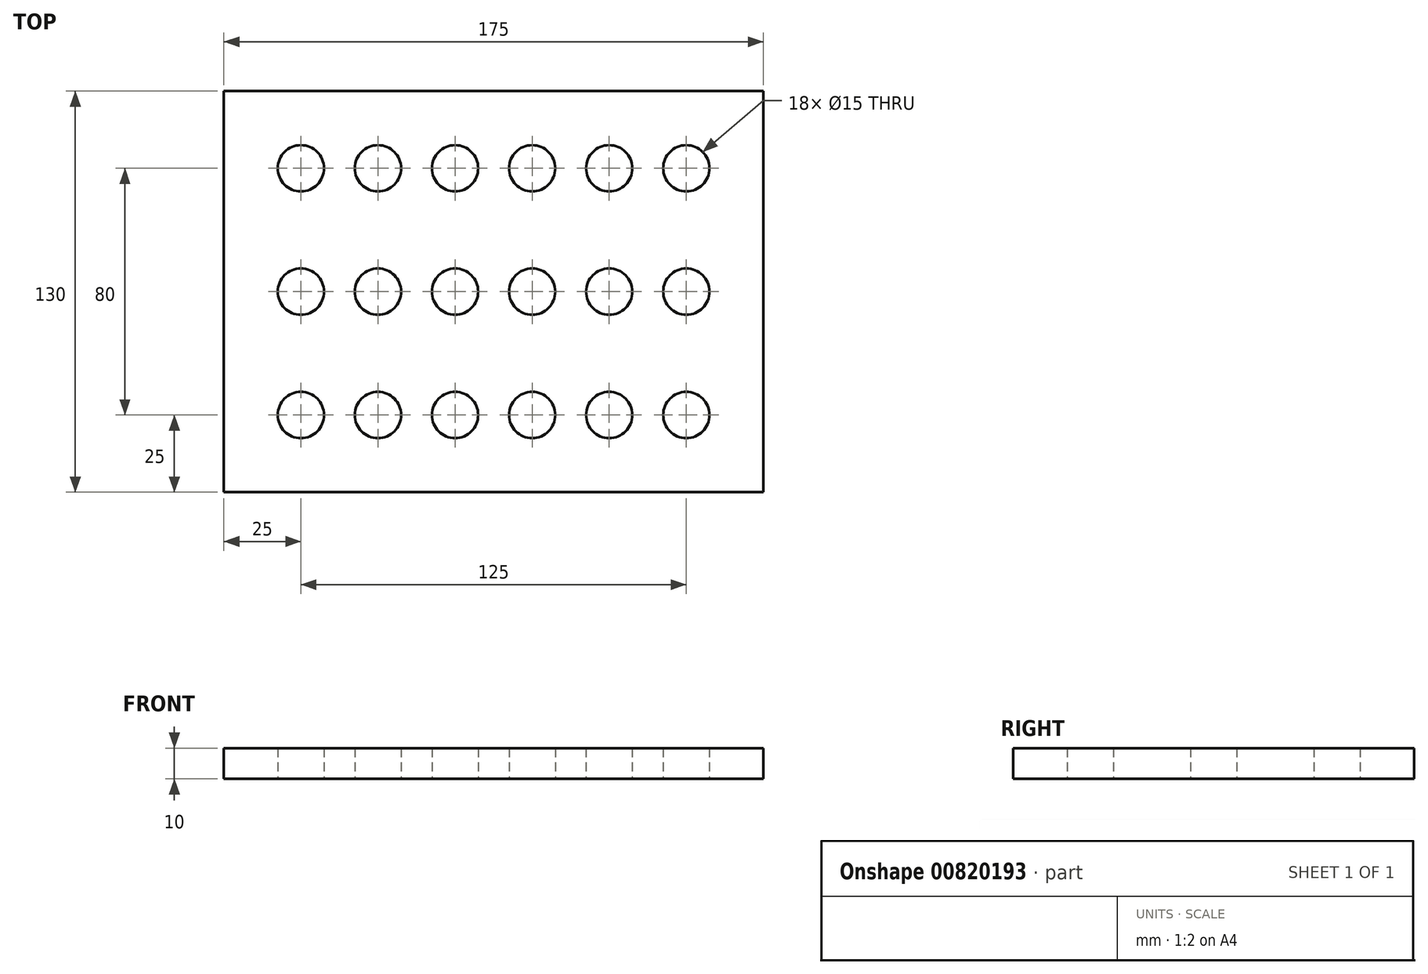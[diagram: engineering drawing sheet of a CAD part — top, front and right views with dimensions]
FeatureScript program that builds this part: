
annotation { "Feature Type Name" : "Feature", "Feature Type Description" : "" }
export const myFeature = defineFeature(function(context is Context, id is Id, definition is map)
    precondition{}
    {
        {
            var Q0;
            Q0=qCreatedBy(makeId("Top.planeOp"),FACE);
            var sketch = newSketch(context, id + "F0", { "sketchPlane" : qUnion([Q0])});
            skLineSegment(sketch, "E0.bottom", {"start": v(-87.5, 65) * mm, "end": v(87.5, 65) * mm});
            skLineSegment(sketch, "E0.top", {"start": v(-87.5, -65) * mm, "end": v(87.5, -65) * mm});
            skLineSegment(sketch, "E0.left", {"start": v(-87.5, 65) * mm, "end": v(-87.5, -65) * mm});
            skLineSegment(sketch, "E0.right", {"start": v(87.5, 65) * mm, "end": v(87.5, -65) * mm});
            skPoint(sketch, "E0.middle", {"position": v(0, 0) * mm});
            skCircle(sketch, "E1", {"center": v(-62.5, 40) * mm, "radius": 7.5 * mm});
            skCircle(sketch, "E2.0.1.0", {"center": v(-62.5, 0) * mm, "radius": 7.5 * mm});
            skCircle(sketch, "E2.0.2.0", {"center": v(-62.5, -40) * mm, "radius": 7.5 * mm});
            skCircle(sketch, "E2.1.0.0", {"center": v(-37.5, 40) * mm, "radius": 7.5 * mm});
            skCircle(sketch, "E2.1.1.0", {"center": v(-37.5, 0) * mm, "radius": 7.5 * mm});
            skCircle(sketch, "E2.1.2.0", {"center": v(-37.5, -40) * mm, "radius": 7.5 * mm});
            skCircle(sketch, "E2.2.0.0", {"center": v(-12.5, 40) * mm, "radius": 7.5 * mm});
            skCircle(sketch, "E2.2.1.0", {"center": v(-12.5, 0) * mm, "radius": 7.5 * mm});
            skCircle(sketch, "E2.2.2.0", {"center": v(-12.5, -40) * mm, "radius": 7.5 * mm});
            skCircle(sketch, "E2.3.0.0", {"center": v(12.5, 40) * mm, "radius": 7.5 * mm});
            skCircle(sketch, "E2.3.1.0", {"center": v(12.5, 0) * mm, "radius": 7.5 * mm});
            skCircle(sketch, "E2.3.2.0", {"center": v(12.5, -40) * mm, "radius": 7.5 * mm});
            skCircle(sketch, "E2.4.0.0", {"center": v(37.5, 40) * mm, "radius": 7.5 * mm});
            skCircle(sketch, "E2.4.1.0", {"center": v(37.5, 0) * mm, "radius": 7.5 * mm});
            skCircle(sketch, "E2.4.2.0", {"center": v(37.5, -40) * mm, "radius": 7.5 * mm});
            skCircle(sketch, "E2.5.0.0", {"center": v(62.5, 40) * mm, "radius": 7.5 * mm});
            skCircle(sketch, "E2.5.1.0", {"center": v(62.5, 0) * mm, "radius": 7.5 * mm});
            skCircle(sketch, "E2.5.2.0", {"center": v(62.5, -40) * mm, "radius": 7.5 * mm});
            skLineSegment(sketch, "E2.direction1", {"start": v(-62.5, 40) * mm, "end": v(-37.5, 40) * mm, "construction": true});
            skLineSegment(sketch, "E2.direction2", {"start": v(-62.5, 40) * mm, "end": v(-62.5, 0) * mm, "construction": true});
            skSolve(sketch);
        }
        {
            var Q0;
            Q0=makeQuery(id+"F0.imprint","IMPRINT",FACE,{"disambiguationData":[TD([[makeQuery(id+"F0.imprint","IMPRINT",EDGE,{"derivedFrom":sQuery(id+"F0.wireOp",EDGE,"E0.bottom")}),-1.0]])]});
            extrude(context, id + "F1", {"entities" : qUnion([Q0]), "depth" : 10 * mm, "offsetDistance" : 25.4 * mm});
        }
    });
